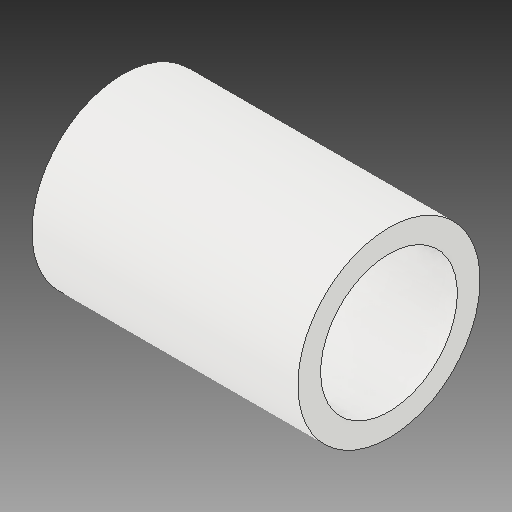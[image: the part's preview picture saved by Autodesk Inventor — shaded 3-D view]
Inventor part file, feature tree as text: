
AUTODESK INVENTOR PART (.ipt)
format: ipt  version: 2019 (Build 230136000, 136)  size: 110,592 bytes
history: native  units: mm
features: extrude x1, sketch x1
ambient origin geometry x8: Origin, YZ Plane, XZ Plane, XY Plane, X Axis, Y Axis, Z Axis, Center Point
bodies: Solid1 (feature_tree)
feature tree (2):
  extrude  "Extrusion1"  Depth=23.351mm
  sketch  "Sketch1"  dims[d1=16.0mm d2=12.0mm d3=23.351mm d4=0.0mm]
